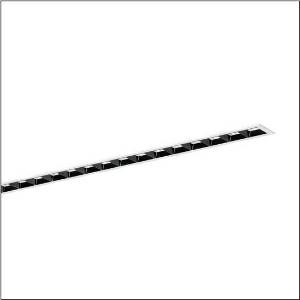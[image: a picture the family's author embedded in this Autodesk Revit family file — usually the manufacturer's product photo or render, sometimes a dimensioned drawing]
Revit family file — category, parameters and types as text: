
# Revit family: silica_r__21_51mx11dc4awb_441a
name_source: partatom
category: Lighting Fixtures
units: mm (PartAtom-declared; Revit-internal decimal feet)

## family parameters
Cut with Voids When Loaded = No
Host = Face
Light Source = No
Part Type = Normal
Room Calculation Point = No
Round Connector Dimension = Use Diameter
Shared = No

## types (1)
- --- (1 x LED, 10800 lm, 64.8 W, 4000K)
    Apparent Load = 65 VA
    CIE Flux Codes = 87 99 100 100 100
    Color Rendering = 80
    Color Temperature = 4000K
    Default Elevation = 1800 mm
    Description = Silica® 21, office luminaire, primary light control with darklight reflector, of PMMA, black, CAT 2 (L<= 3000cd/m²), light emission: direct distribution, primary light characteristic: symmetric, installation type: recessed, LED, rated luminous flux: 10.800lm, luminous efficacy: 167lm/W, light colour: 840, colour temperature: 4000K, control gear: DALI 2, with terminal, 3+2-pole, max. 2.5mm², mains connection: 220..240V, AC, 50/60Hz, rated input power: 64.8W, luminaire housing, of aluminium, traffic white (RAL 9016), length: 3.028mm, width: 79mm, height: 53mm, protection rating (complete): IP20, insulation class (complete): insulation class I (protective earthing), certification: CE, ENEC, VDE, permissible operating ambient temperature: 0..+35°C, standard: EN 50419, packaging unit: 1 piece
    Height = 0 mm  [stored 0 ft]
    Lamp = 1 x LED
    Lamp Light Flux = 10800 lm
    Lamp Power = 64.8 W
    Lamp count = 1
    Length = 3027 mm
    Luminous efficacy = 167 lm/W
    Manufacturer = Siteco
    ModVariant = No
    Model = 51MX11DC4AWB
    Mounting Place = Ceiling
    Mounting Type = Recessed
    Number of Poles = 1
    OnlyDefault = Yes
    Power Factor = 1
    Product Name = Silica® 21
    Product group = office luminaire | ceiling recessed
    ProductGroupID = 400
    Protection Class = Protection class I
    Protection Degree = IP 20
    RLX_Detail_Level = 1
    RLX_Emergency_Light_Flux = 0 lm
    RLX_Emergency_Type = 0
    RLX_Emergency_Type_DB = No
    RlxData = <blob elided: 62745 chars, md5=c9d43ad7>
    Socket = socket
    Standby Power = 0 W
    System Light Flux = 10800 lm
    System Power = 65 W
    Type Comments = factory setting: luminous flux: 100 % | dim-lin: 254 | 367 mA
    Type Image = l_1335880.jpg
    URL = http://relux.com
    VarID = @adj_144891
    Voltage = 0 V
    Weight = 0.00 kg
    Width = 79 mm

note: [stored X ft] marks values corroborated as IEEE doubles in the binary element streams (Revit-internal decimal feet)

## geometry (parser evidence)
native form markers: Blend x4, Sweep x11
no freeform markers — native parametric forms only
